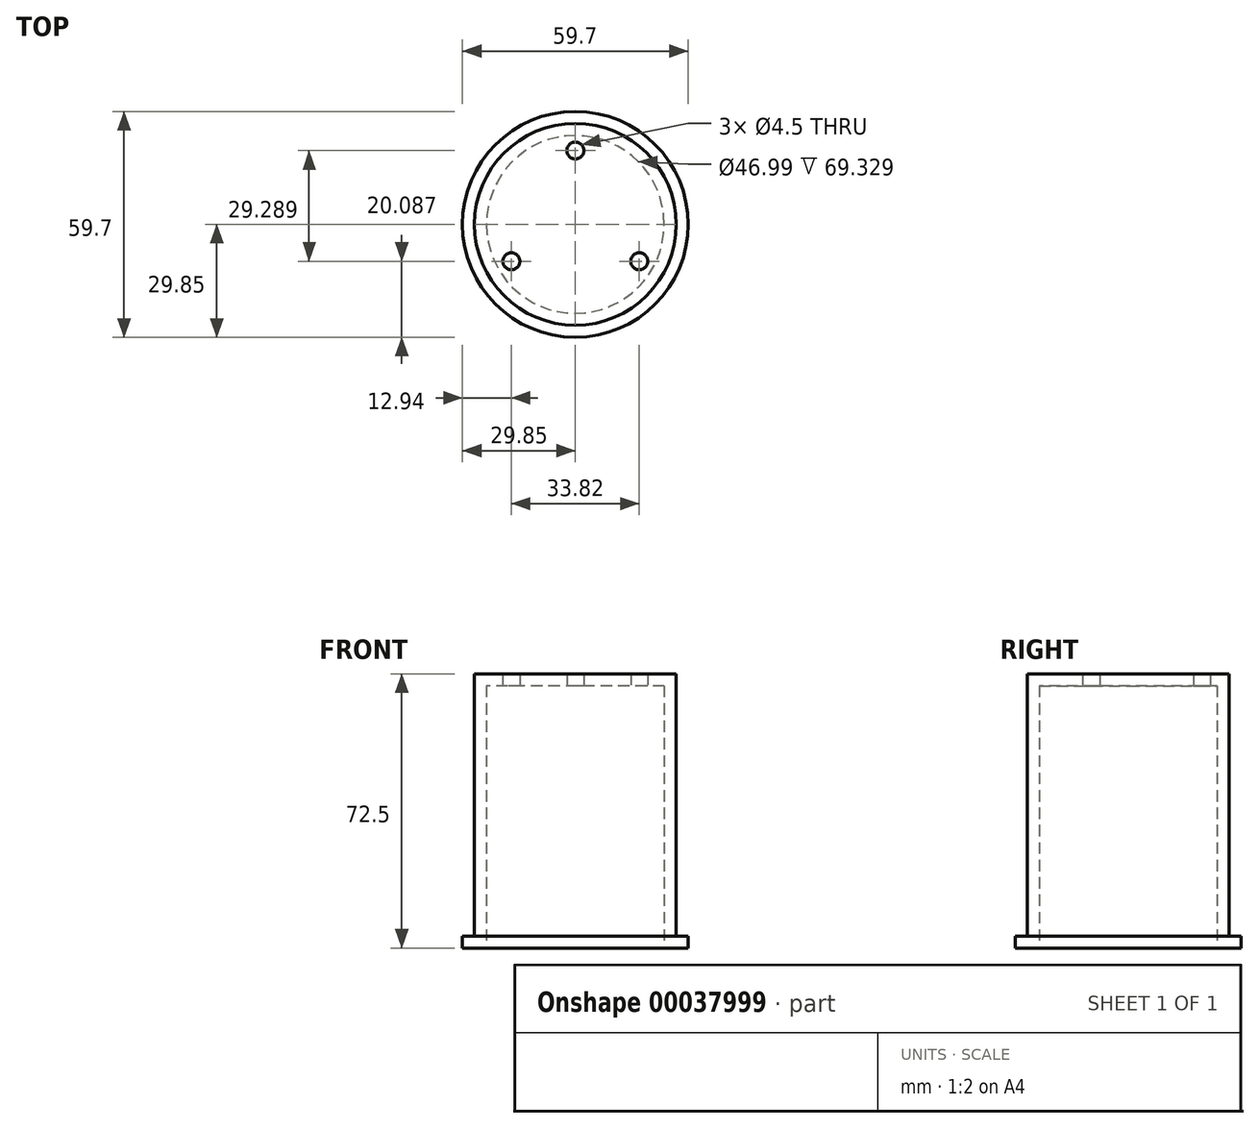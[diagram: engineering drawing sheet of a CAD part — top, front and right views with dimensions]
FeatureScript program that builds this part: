
annotation { "Feature Type Name" : "Feature", "Feature Type Description" : "" }
export const myFeature = defineFeature(function(context is Context, id is Id, definition is map)
    precondition{}
    {
        {
            var Q0;
            Q0=qCreatedBy(makeId("Top.planeOp"),FACE);
            var sketch = newSketch(context, id + "F0", { "sketchPlane" : qUnion([Q0])});
            skCircle(sketch, "E0", {"center": v(0, 0) * mm, "radius": 29.85 * mm});
            skCircle(sketch, "E1", {"center": v(0, 0) * mm, "radius": 23.5 * mm});
            skSolve(sketch);
        }
        {
            var Q0;
            Q0 = qSketchRegion(id + "F0", true);
            extrude(context, id + "F1", {"entities" : qUnion([Q0]), "depth" : 3.17 * mm});
        }
        {
            var Q0;
            Q0=makeQuery(id+"F1.opExtrude","CAP_FACE",FACE,{"disambiguationData":[OSD([sQuery(id+"F0.wireOp",EDGE,"E0"),sQuery(id+"F0.wireOp",EDGE,"E1")])],"isStart":false});
            var sketch = newSketch(context, id + "F2", { "sketchPlane" : qUnion([Q0])});
            skCircle(sketch, "E2", {"center": v(0, 0) * mm, "radius": 23.5 * mm});
            skCircle(sketch, "E3", {"center": v(0, 0) * mm, "radius": 26.67 * mm});
            skSolve(sketch);
        }
        {
            var Q0;
            Q0 = qSketchRegion(id + "F2", true);
            extrude(context, id + "F3", {"entities" : qUnion([Q0]), "operationType" : NewBodyOperationType.ADD, "depth" : 66.15 * mm});
        }
        {
            var Q0;
            Q0=makeQuery(id+"F3.opExtrude","CAP_FACE",FACE,{"disambiguationData":[OSD([sQuery(id+"F2.wireOp",EDGE,"E2"),sQuery(id+"F2.wireOp",EDGE,"E3")])],"isStart":false});
            var sketch = newSketch(context, id + "F4", { "sketchPlane" : qUnion([Q0])});
            skCircle(sketch, "E4", {"center": v(0, 0) * mm, "radius": 26.67 * mm});
            skCircle(sketch, "E5.cCircle", {"center": v(0, 0) * mm, "radius": 9.76 * mm, "construction": true});
            skLineSegment(sketch, "E5.0", {"start": v(16.91, -9.76) * mm, "end": v(-16.91, -9.76) * mm, "construction": true});
            skLineSegment(sketch, "E5.1", {"start": v(-16.91, -9.76) * mm, "end": v(0, 19.53) * mm, "construction": true});
            skLineSegment(sketch, "E5.2", {"start": v(0, 19.53) * mm, "end": v(16.91, -9.76) * mm, "construction": true});
            skPoint(sketch, "E5.0.midPoint", {"position": v(0, -9.76) * mm});
            skCircle(sketch, "E6", {"center": v(0, 19.53) * mm, "radius": 3.97 * mm, "construction": true});
            skCircle(sketch, "E7", {"center": v(0, 19.53) * mm, "radius": 2.25 * mm});
            skCircle(sketch, "E8", {"center": v(-16.91, -9.76) * mm, "radius": 2.25 * mm});
            skCircle(sketch, "E9", {"center": v(16.91, -9.76) * mm, "radius": 2.25 * mm});
            skSolve(sketch);
        }
        {
            var Q0;
            Q0 = qSketchRegion(id + "F4", true);
            extrude(context, id + "F5", {"entities" : qUnion([Q0]), "operationType" : NewBodyOperationType.ADD, "depth" : 3.17 * mm});
        }
    });
